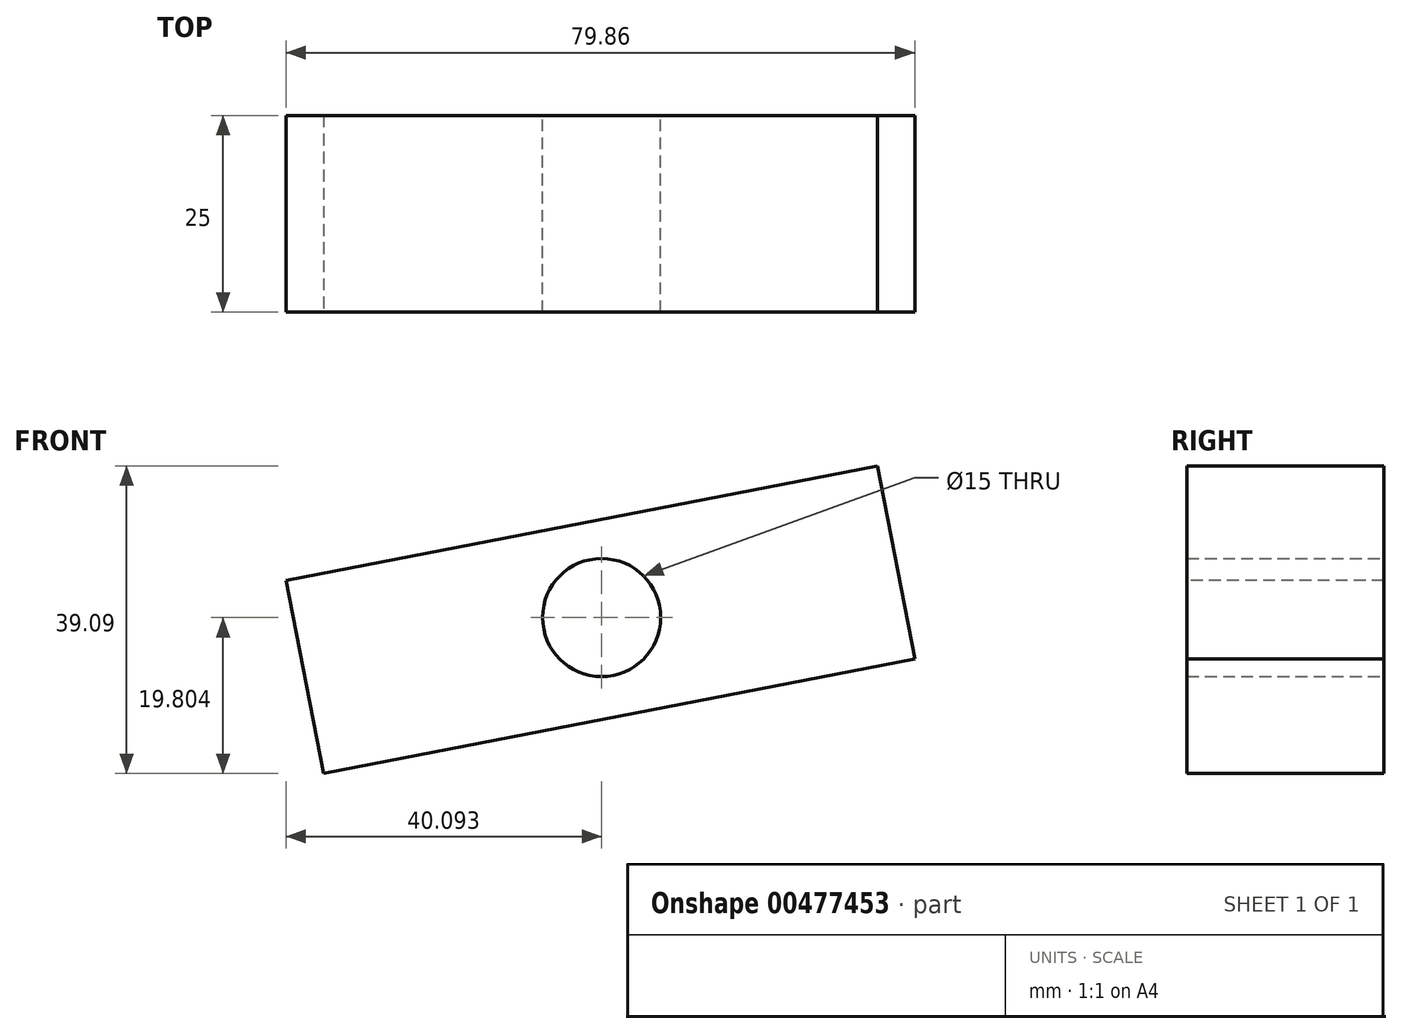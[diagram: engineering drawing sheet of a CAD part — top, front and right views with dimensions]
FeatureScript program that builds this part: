
annotation { "Feature Type Name" : "Feature", "Feature Type Description" : "" }
export const myFeature = defineFeature(function(context is Context, id is Id, definition is map)
    precondition{}
    {
        {
            var Q0;
            Q0=qCreatedBy(makeId("Front.planeOp"),FACE);
            var sketch = newSketch(context, id + "F0", { "sketchPlane" : qUnion([Q0])});
            skLineSegment(sketch, "E0", {"start": v(-119.07, 45.78) * mm, "end": v(-43.96, 60.33) * mm});
            skLineSegment(sketch, "E1", {"start": v(-38.2, 56.76) * mm, "end": v(-15.6, -24.5) * mm});
            skPoint(sketch, "E2.visualSharp", {"position": v(-39.43, 61.2) * mm});
            skArc(sketch, "E2.filletArc", {"start": v(-38.2, 56.76) * mm, "mid": v(-40.38, 59.67) * mm, "end": v(-43.96, 60.33) * mm});
            skSolve(sketch);
        }
        {
            var Q0;
            Q0=sQuery(id+"F0.wireOp",EDGE,"E1");
            var Q1;
            Q1=sQuery(id+"F0.wireOp",EDGE,"E0");
            var Q2;
            Q2=sQuery(id+"F0.wireOp",EDGE,"E2.filletArc");
            extrude(context, id + "F1", {"bodyType" : ToolBodyType.SURFACE, "surfaceEntities" : qUnion([Q0, Q1, Q2]), "depth" : 25 * mm});
        }
        {
            var Q0;
            Q0=makeQuery(id+"F1.opExtrude","SWEPT_FACE",FACE,{"disambiguationData":[OSD([sQuery(id+"F0.wireOp",EDGE,"E0")])]});
            extrude(context, id + "F2", {"entities" : qUnion([Q0]), "depth" : 25 * mm});
        }
        {
            var Q0;
            {var subQ0=sQuery(id+"F0.wireOp",EDGE,"E0");Q0=makeQuery(id+"F2.opExtrude","SWEPT_FACE",FACE,{"disambiguationData":[OSD([subQ0]),TDD([makeQuery(id+"F1.opExtrude","CAP_EDGE",EDGE,{"disambiguationData":[OSD([subQ0])],"isStart":true})])]});}
            var sketch = newSketch(context, id + "F3", { "sketchPlane" : qUnion([Q0])});
            skPoint(sketch, "E3", {"position": v(78.98, 41.04) * mm});
            skSolve(sketch);
        }
        {
            var Q0;
            Q0=sQuery(id+"F3.wireOp",VERTEX,"E3");
            var Q1;
            Q1=makeQuery(id+"F2.opExtrude","SWEPT_BODY",BODY,{"disambiguationData":[OSD([sQuery(id+"F0.wireOp",EDGE,"E0")])]});
            hole(context, id + "F4", {"style" : HoleStyle.SIMPLE, "endStyle" : HoleEndStyle.THROUGH, "holeDiameter" : 15 * mm, "isTappedThrough" : true, "tappedDepth" : 12 * mm, "tapClearance" : 3, "startFromSketch" : true, "locations" : qUnion([Q0]), "scope" : qUnion([Q1])});
        }
    });
